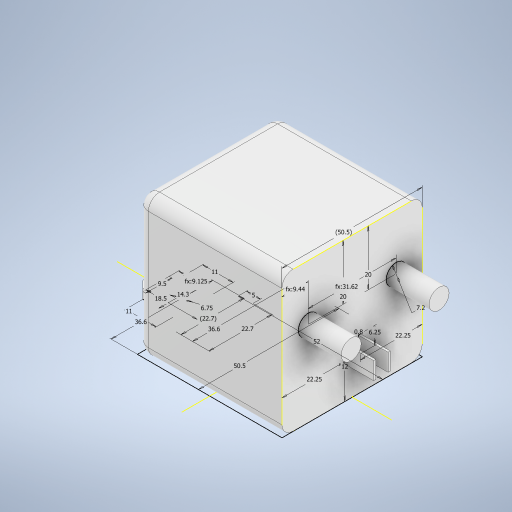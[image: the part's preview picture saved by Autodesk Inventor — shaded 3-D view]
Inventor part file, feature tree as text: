
AUTODESK INVENTOR PART (.ipt)
format: ipt  version: 2023 (Build 270158000, 158)  size: 326,656 bytes
history: native  units: in
note: dims shown in document units (in); Inventor stores cm internally (conversion verified against a paired STEP export)
features: extrude x4, sketch x2, fillet x2
ambient origin geometry x8: Origin, YZ Plane, XZ Plane, XY Plane, X Axis, Y Axis, Z Axis, Center Point
bodies: Solid1 (feature_tree)
feature tree (8):
  sketch  "Sketch1"  dims[d1=2.0472in d2=1.9882in]
  extrude  "Extrusion1"  Depth=1.9882in
  extrude  "Extrusion2"  Depth=0.1575in
  fillet  "Fillet1"  Radius=1.4409in
  sketch  "Sketch2"  dims[d3=0.563in d4=1.4409in d5=1.4409in d6=0.7283in d7=0.374in d8=0.4331in d9=0.4331in d10=0.8937in d11=0.2657in d12=0.3593in d14=0.1378in d15=0.0in d16=1.9882in d17=0.0in d18=0.1575in d19=0.2835in d20=0.2461in d21=0.0315in d22=0.4724in d23=0.876in d24=0.876in d25=1.2449in d26=0.3717in d27=1.9882in d28=0.7874in d29=0.7874in d30=0.6102in d31=0.0in d32=0.4232in d33=0.0in d34=0.1969in d35=0.8937in d36=0.1575in]
  extrude  "Extrusion3"  Depth=0.7283in
  extrude  "Extrusion4"  Depth=0.1575in
  fillet  "Fillet2"  Radius=0.4331in
